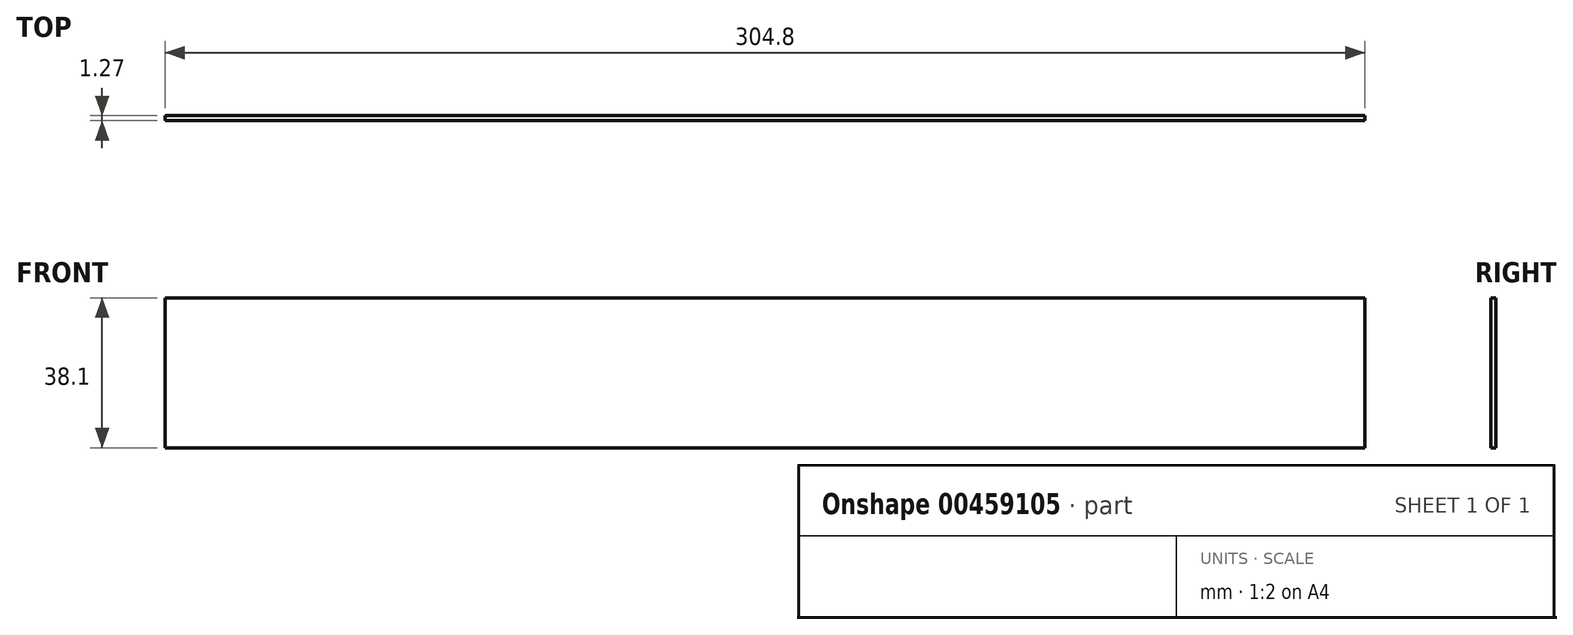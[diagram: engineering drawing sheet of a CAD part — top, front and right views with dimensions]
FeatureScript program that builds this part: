
annotation { "Feature Type Name" : "Feature", "Feature Type Description" : "" }
export const myFeature = defineFeature(function(context is Context, id is Id, definition is map)
    precondition{}
    {
        {
            var Q0;
            Q0=qCreatedBy(makeId("Front.planeOp"),FACE);
            var sketch = newSketch(context, id + "F0", { "sketchPlane" : qUnion([Q0])});
            skLineSegment(sketch, "E0.bottom", {"start": v(-19.05, 18.61) * mm, "end": v(285.75, 18.61) * mm});
            skLineSegment(sketch, "E0.top", {"start": v(-19.05, -19.49) * mm, "end": v(285.75, -19.49) * mm});
            skLineSegment(sketch, "E0.left", {"start": v(-19.05, 18.61) * mm, "end": v(-19.05, -19.49) * mm});
            skLineSegment(sketch, "E0.right", {"start": v(285.75, 18.61) * mm, "end": v(285.75, -19.49) * mm});
            skSolve(sketch);
        }
        {
            var Q0;
            Q0=makeQuery(id+"F0.imprint","IMPRINT",FACE,{"disambiguationData":[TD([[makeQuery(id+"F0.imprint","IMPRINT",EDGE,{"derivedFrom":sQuery(id+"F0.wireOp",EDGE,"E0.bottom")}),-1.0]])]});
            extrude(context, id + "F1", {"entities" : qUnion([Q0]), "depth" : 1.27 * mm});
        }
    });
